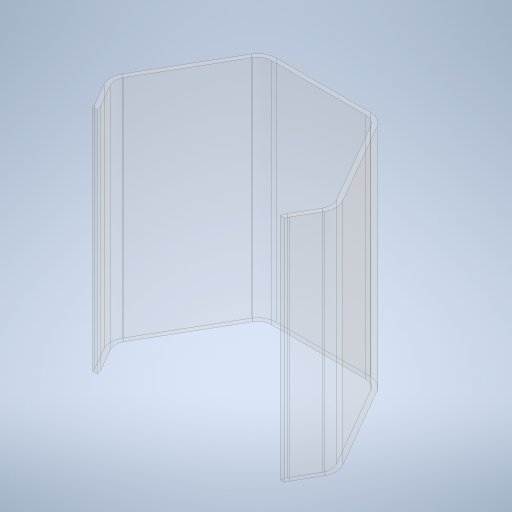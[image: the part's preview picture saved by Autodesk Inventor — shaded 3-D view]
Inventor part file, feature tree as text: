
AUTODESK INVENTOR PART (.ipt)
format: ipt  version: 2024 (Build 280153000, 153)  size: 452,096 bytes
history: native  units: mm
features: extrude x9, sketch x9, projected_geometry x3, fillet x1
ambient origin geometry x8: Origin, YZ Plane, XZ Plane, XY Plane, X Axis, Y Axis, Z Axis, Center Point
bodies: Solid1 (feature_tree)
feature tree (22):
  extrude  "Extrusion1"  Depth=10.0mm
  extrude  "Extrusion2"  Depth=20.0mm TaperAngle=0.0deg
  sketch  "Sketch3"  dims[d8=34.0mm d9=5.0mm d10=0.0mm]
  sketch  "Sketch4"  dims[d12=60.0mm d13=360.0deg d14=22.0mm d15=0.0mm]
  extrude  "Extrusion3"  Depth=5.0mm TaperAngle=0.0deg
  extrude  "Extrusion4"  Depth=22.0mm TaperAngle=0.0deg
  extrude  "Extrusion5"  Depth=20.0mm TaperAngle=0.0deg
  fillet  "Fillet1"  Radius=150.0mm
  extrude  "Extrusion6"  Depth=12.0mm
  extrude  "Extrusion7"  Depth=20.0mm
  extrude  "Extrusion8"  Depth=12.0mm
  extrude  "Extrusion9"  Depth=200.0mm TaperAngle=360.0deg
  sketch  "Sketch1"  dims[d0=250.0mm d1=160.0mm d2=160.0mm d3=10.0mm d4=52.0mm]
  sketch  "Sketch2"  dims[d5=80.0mm d6=20.0mm d7=0.0mm]
  sketch  "Sketch5"  dims[d17=60.0mm d18=360.0deg d19=20.0mm d20=0.0mm d21=150.0mm]
  sketch  "Sketch6"  dims[d22=5.0mm d23=0.0mm d24=12.0mm]
  projected_geometry  "Projected Loop1"
  sketch  "Sketch7"  dims[d25=20.0mm d26=20.0mm]
  sketch  "Sketch8"  dims[d27=12.0mm d28=0.0mm d29=84.286mm]
  projected_geometry  "Projected Loop2"
  sketch  "Sketch9"  dims[d30=10.0mm d31=240.0mm d33=360.0deg d35=39.0mm d36=0.0mm d37=4.0mm d38=200.0mm d39=0.0mm d40=200.0mm d41=0.0mm]
  projected_geometry  "Projected Loop3"
